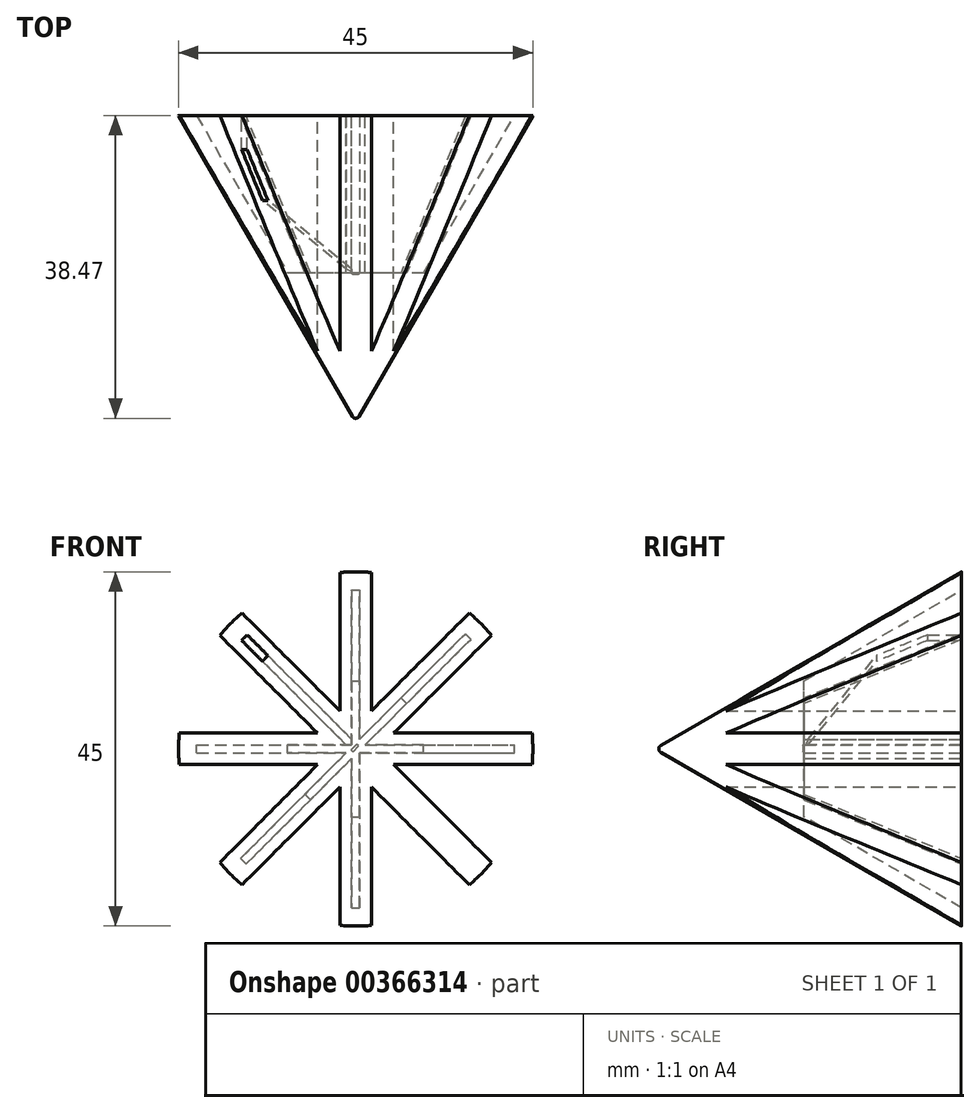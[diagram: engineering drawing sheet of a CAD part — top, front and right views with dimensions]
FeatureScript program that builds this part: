
annotation { "Feature Type Name" : "Feature", "Feature Type Description" : "" }
export const myFeature = defineFeature(function(context is Context, id is Id, definition is map)
    precondition{}
    {
        {
            var Q0;
            Q0=qCreatedBy(makeId("Front.planeOp"),FACE);
            var sketch = newSketch(context, id + "F0", { "sketchPlane" : qUnion([Q0])});
            skCircle(sketch, "E0.cCircle", {"center": v(0, 0) * mm, "radius": 20.79 * mm, "construction": true});
            skLineSegment(sketch, "E0.0", {"start": v(-22.5, 0) * mm, "end": v(-15.9, 15.9) * mm});
            skLineSegment(sketch, "E0.1", {"start": v(-15.9, 15.9) * mm, "end": v(0, 22.5) * mm});
            skLineSegment(sketch, "E0.2", {"start": v(0, 22.5) * mm, "end": v(15.9, 15.9) * mm});
            skLineSegment(sketch, "E0.3", {"start": v(15.9, 15.9) * mm, "end": v(22.5, 0) * mm});
            skLineSegment(sketch, "E0.4", {"start": v(22.5, 0) * mm, "end": v(15.9, -15.9) * mm});
            skLineSegment(sketch, "E0.5", {"start": v(15.9, -15.9) * mm, "end": v(0, -22.5) * mm});
            skLineSegment(sketch, "E0.6", {"start": v(0, -22.5) * mm, "end": v(-15.9, -15.9) * mm});
            skLineSegment(sketch, "E0.7", {"start": v(-15.9, -15.9) * mm, "end": v(-22.5, 0) * mm});
            skLineSegment(sketch, "E1", {"start": v(0, 22.5) * mm, "end": v(0, -22.5) * mm});
            skLineSegment(sketch, "E2", {"start": v(-15.9, -15.9) * mm, "end": v(15.9, 15.9) * mm});
            skLineSegment(sketch, "E3", {"start": v(-15.9, 15.9) * mm, "end": v(15.9, -15.9) * mm});
            skLineSegment(sketch, "E4", {"start": v(22.5, 0) * mm, "end": v(-22.5, 0) * mm});
            skSolve(sketch);
        }
        {
            var Q0;
            Q0=qCreatedBy(makeId("Top.planeOp"),FACE);
            var sketch = newSketch(context, id + "F1", { "sketchPlane" : qUnion([Q0])});
            skLineSegment(sketch, "E5", {"start": v(-22.5, 0) * mm, "end": v(0, -38.97) * mm});
            skLineSegment(sketch, "E6", {"start": v(0, -38.97) * mm, "end": v(22.5, 0) * mm});
            skLineSegment(sketch, "E7", {"start": v(22.5, 0) * mm, "end": v(-22.5, 0) * mm});
            skLineSegment(sketch, "E8", {"start": v(0, -69.99) * mm, "end": v(0, 32.44) * mm, "construction": true});
            skSolve(sketch);
        }
        {
            var Q0;
            Q0=makeQuery(id+"F1.imprint","IMPRINT",FACE,{"disambiguationData":[TD([[makeQuery(id+"F1.imprint","IMPRINT",EDGE,{"derivedFrom":sQuery(id+"F1.wireOp",EDGE,"E5")}),1.0]])]});
            extrude(context, id + "F2", {"entities" : qUnion([Q0]), "depth" : 2 * mm, "hasSecondDirection" : true, "secondDirectionOppositeDirection" : true, "secondDirectionDepth" : 2 * mm});
        }
        {
            var Q0;
            Q0=makeQuery(id+"F2.opExtrude","SWEPT_BODY",BODY,{"disambiguationData":[OSD([sQuery(id+"F1.wireOp",EDGE,"E5"),sQuery(id+"F1.wireOp",EDGE,"E6"),sQuery(id+"F1.wireOp",EDGE,"E7")])]});
            var Q1;
            Q1=sQuery(id+"F1.wireOp",EDGE,"E8");
            transform(context, id + "F3", {"entities" : qUnion([Q0]), "transformType" : TransformType.ROTATION, "transformAxis" : qUnion([Q1]), "angle" : 45 * degree, "makeCopy" : true});
        }
        {
            var Q0;
            Q0=makeQuery(id+"F3.opPattern","COPY",BODY,{"derivedFrom":makeQuery(id+"F2.opExtrude","SWEPT_BODY",BODY,{"disambiguationData":[OSD([sQuery(id+"F1.wireOp",EDGE,"E5"),sQuery(id+"F1.wireOp",EDGE,"E6"),sQuery(id+"F1.wireOp",EDGE,"E7")])]}),"instanceName":"1"});
            var Q1;
            Q1=sQuery(id+"F1.wireOp",EDGE,"E8");
            transform(context, id + "F4", {"entities" : qUnion([Q0]), "transformType" : TransformType.ROTATION, "transformAxis" : qUnion([Q1]), "angle" : 45 * degree, "makeCopy" : true});
        }
        {
            var Q0;
            Q0=makeQuery(id+"F4.opPattern","COPY",BODY,{"derivedFrom":makeQuery(id+"F3.opPattern","COPY",BODY,{"derivedFrom":makeQuery(id+"F2.opExtrude","SWEPT_BODY",BODY,{"disambiguationData":[OSD([sQuery(id+"F1.wireOp",EDGE,"E5"),sQuery(id+"F1.wireOp",EDGE,"E6"),sQuery(id+"F1.wireOp",EDGE,"E7")])]}),"instanceName":"1"}),"instanceName":"1"});
            var Q1;
            Q1=sQuery(id+"F1.wireOp",EDGE,"E8");
            transform(context, id + "F5", {"entities" : qUnion([Q0]), "transformType" : TransformType.ROTATION, "transformAxis" : qUnion([Q1]), "angle" : 45 * degree, "makeCopy" : true});
        }
        {
            var Q0;
            Q0=makeQuery(id+"F2.opExtrude","SWEPT_BODY",BODY,{"disambiguationData":[OSD([sQuery(id+"F1.wireOp",EDGE,"E5"),sQuery(id+"F1.wireOp",EDGE,"E6"),sQuery(id+"F1.wireOp",EDGE,"E7")])]});
            var Q1;
            Q1=makeQuery(id+"F3.opPattern","COPY",BODY,{"derivedFrom":makeQuery(id+"F2.opExtrude","SWEPT_BODY",BODY,{"disambiguationData":[OSD([sQuery(id+"F1.wireOp",EDGE,"E5"),sQuery(id+"F1.wireOp",EDGE,"E6"),sQuery(id+"F1.wireOp",EDGE,"E7")])]}),"instanceName":"1"});
            var Q2;
            Q2=makeQuery(id+"F4.opPattern","COPY",BODY,{"derivedFrom":makeQuery(id+"F3.opPattern","COPY",BODY,{"derivedFrom":makeQuery(id+"F2.opExtrude","SWEPT_BODY",BODY,{"disambiguationData":[OSD([sQuery(id+"F1.wireOp",EDGE,"E5"),sQuery(id+"F1.wireOp",EDGE,"E6"),sQuery(id+"F1.wireOp",EDGE,"E7")])]}),"instanceName":"1"}),"instanceName":"1"});
            var Q3;
            Q3=makeQuery(id+"F5.opPattern","COPY",BODY,{"derivedFrom":makeQuery(id+"F4.opPattern","COPY",BODY,{"derivedFrom":makeQuery(id+"F3.opPattern","COPY",BODY,{"derivedFrom":makeQuery(id+"F2.opExtrude","SWEPT_BODY",BODY,{"disambiguationData":[OSD([sQuery(id+"F1.wireOp",EDGE,"E5"),sQuery(id+"F1.wireOp",EDGE,"E6"),sQuery(id+"F1.wireOp",EDGE,"E7")])]}),"instanceName":"1"}),"instanceName":"1"}),"instanceName":"1"});
            booleanBodies(context, id + "F6", {"operationType" : BooleanOperationType.UNION, "tools" : qUnion([Q0, Q1, Q2, Q3])});
        }
        {
            var Q0;
            Q0=qCreatedBy(makeId("Right.planeOp"),FACE);
            var Q1;
            Q1=sQuery(id+"F1.wireOp",EDGE,"E8");
            cPlane(context, id + "F7", {"entities" : qUnion([Q0, Q1]), "cplaneType" : CPlaneType.LINE_ANGLE, "offset" : 25 * mm, "angle" : 45 * degree, "width" : 150 * mm, "height" : 150 * mm});
        }
        {
            var Q0;
            Q0=qCreatedBy(makeId("Top.planeOp"),FACE);
            var Q1;
            Q1=sQuery(id+"F1.wireOp",EDGE,"E8");
            cPlane(context, id + "F8", {"entities" : qUnion([Q0, Q1]), "cplaneType" : CPlaneType.LINE_ANGLE, "offset" : 25 * mm, "angle" : 45 * degree, "width" : 150 * mm, "height" : 150 * mm});
        }
        {
            var Q0;
            Q0=qCreatedBy(id+"F7.planeOp",FACE);
            var sketch = newSketch(context, id + "F9", { "sketchPlane" : qUnion([Q0])});
            skLineSegment(sketch, "E9", {"start": v(20, -8.64) * mm, "end": v(0, -20.2) * mm});
            skLineSegment(sketch, "E10", {"start": v(0, -20.2) * mm, "end": v(0, 20.2) * mm});
            skLineSegment(sketch, "E11", {"start": v(0, 20.2) * mm, "end": v(20, 8.64) * mm});
            skLineSegment(sketch, "E12", {"start": v(20, 8.64) * mm, "end": v(20, -8.64) * mm});
            skPoint(sketch, "E13.orphan", {"position": v(34.97, 0) * mm});
            skSolve(sketch);
        }
        {
            var Q0;
            Q0=qSketchRegion(id+"F9",true);
            extrude(context, id + "F10", {"entities" : qUnion([Q0]), "operationType" : NewBodyOperationType.REMOVE, "endBound" : BoundingType.SYMMETRIC, "oppositeDirection" : true, "depth" : 1 * mm});
        }
        {
            var Q0;
            Q0=qCreatedBy(makeId("Right.planeOp"),FACE);
            var sketch = newSketch(context, id + "F11", { "sketchPlane" : qUnion([Q0])});
            skLineSegment(sketch, "E14", {"start": v(0, -20.2) * mm, "end": v(-20, -8.64) * mm});
            skLineSegment(sketch, "E15", {"start": v(-20, 8.64) * mm, "end": v(0, 20.2) * mm});
            skLineSegment(sketch, "E16", {"start": v(0, 20.2) * mm, "end": v(0, -20.2) * mm});
            skLineSegment(sketch, "E17", {"start": v(-20, -8.64) * mm, "end": v(-20, 8.64) * mm});
            skPoint(sketch, "E18.orphan", {"position": v(-34.97, 0) * mm});
            skSolve(sketch);
        }
        {
            var Q0;
            Q0=qSketchRegion(id+"F11",true);
            extrude(context, id + "F12", {"entities" : qUnion([Q0]), "operationType" : NewBodyOperationType.REMOVE, "endBound" : BoundingType.SYMMETRIC, "oppositeDirection" : true, "depth" : 1 * mm});
        }
        {
            var Q0;
            Q0=qCreatedBy(id+"F8.planeOp",FACE);
            var sketch = newSketch(context, id + "F13", { "sketchPlane" : qUnion([Q0])});
            skLineSegment(sketch, "E19", {"start": v(20.2, 0) * mm, "end": v(8.64, 20) * mm});
            skLineSegment(sketch, "E20", {"start": v(-8.64, 20) * mm, "end": v(-20.2, 0) * mm});
            skLineSegment(sketch, "E21", {"start": v(-20.2, 0) * mm, "end": v(20.2, 0) * mm});
            skLineSegment(sketch, "E22", {"start": v(8.64, 20) * mm, "end": v(-8.64, 20) * mm});
            skPoint(sketch, "E23.orphan", {"position": v(0, 34.97) * mm});
            skSolve(sketch);
        }
        {
            var Q0;
            Q0=qCreatedBy(makeId("Top.planeOp"),FACE);
            var sketch = newSketch(context, id + "F14", { "sketchPlane" : qUnion([Q0])});
            skLineSegment(sketch, "E24.0", {"start": v(-20.2, 0) * mm, "end": v(-8.64, -20) * mm});
            skLineSegment(sketch, "E24.2", {"start": v(8.64, -20) * mm, "end": v(20.2, 0) * mm});
            skLineSegment(sketch, "E25", {"start": v(-20.2, 0) * mm, "end": v(20.2, 0) * mm});
            skLineSegment(sketch, "E26", {"start": v(8.64, -20) * mm, "end": v(-8.64, -20) * mm});
            skSolve(sketch);
        }
        {
            var Q0;
            Q0=qSketchRegion(id+"F14",true);
            extrude(context, id + "F15", {"entities" : qUnion([Q0]), "operationType" : NewBodyOperationType.REMOVE, "endBound" : BoundingType.SYMMETRIC, "oppositeDirection" : true, "depth" : 1 * mm});
        }
        {
            var Q0;
            Q0=qCreatedBy(makeId("Top.planeOp"),FACE);
            var sketch = newSketch(context, id + "F16", { "sketchPlane" : qUnion([Q0])});
            skLineSegment(sketch, "E27", {"start": v(22.5, 0) * mm, "end": v(0.43, -38.22) * mm});
            skLineSegment(sketch, "E28", {"start": v(0, -40.97) * mm, "end": v(49.3, -40.97) * mm});
            skLineSegment(sketch, "E29", {"start": v(0, -38.97) * mm, "end": v(0, -40.97) * mm});
            skLineSegment(sketch, "E30", {"start": v(22.5, 0) * mm, "end": v(47.75, 0) * mm});
            skLineSegment(sketch, "E31", {"start": v(47.75, 0) * mm, "end": v(49.3, -40.97) * mm});
            skArc(sketch, "E32", {"start": v(0, -38.47) * mm, "mid": v(0.25, -38.4) * mm, "end": v(0.43, -38.22) * mm});
            skLineSegment(sketch, "E33", {"start": v(0, -38.47) * mm, "end": v(0, -38.97) * mm});
            skSolve(sketch);
        }
        {
            var Q0;
            Q0=makeQuery(id+"F16.imprint","IMPRINT",FACE,{"disambiguationData":[TD([[makeQuery(id+"F16.imprint","IMPRINT",EDGE,{"derivedFrom":sQuery(id+"F16.wireOp",EDGE,"E27")}),1.0]])]});
            var Q1;
            Q1=sQuery(id+"F1.wireOp",EDGE,"E8");
            revolve(context, id + "F17", {"operationType" : NewBodyOperationType.REMOVE, "entities" : qUnion([Q0]), "axis" : qUnion([Q1]), "revolveType" : RevolveType.FULL, "oppositeDirection" : true});
        }
        {
            var Q0;
            Q0=qSketchRegion(id+"F13",true);
            extrude(context, id + "F18", {"entities" : qUnion([Q0]), "operationType" : NewBodyOperationType.REMOVE, "endBound" : BoundingType.SYMMETRIC, "oppositeDirection" : true, "depth" : 1 * mm});
        }
    });
